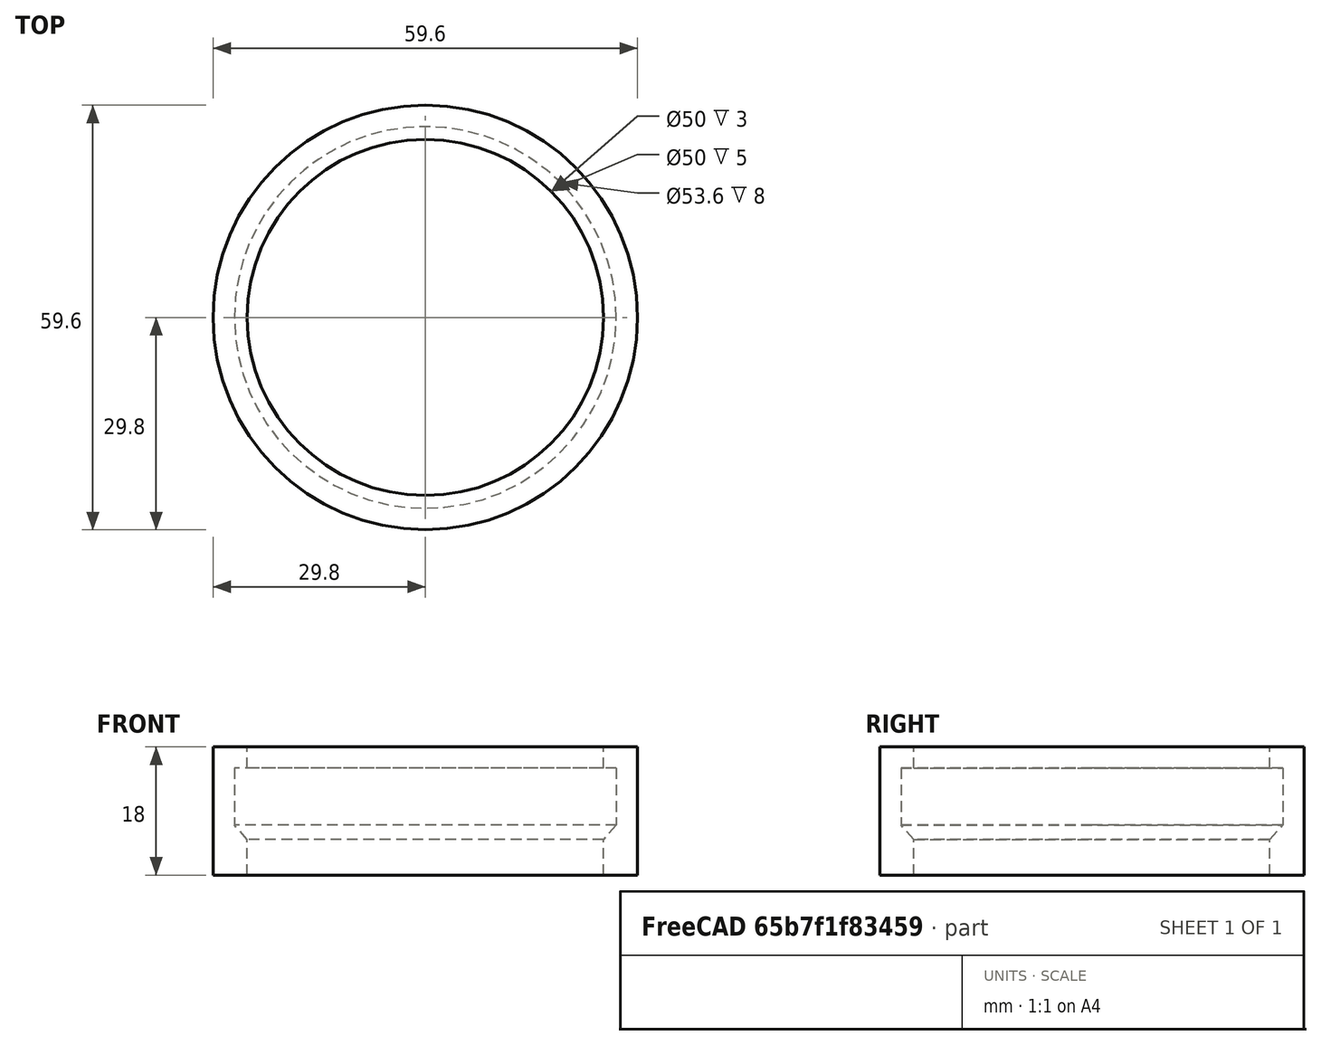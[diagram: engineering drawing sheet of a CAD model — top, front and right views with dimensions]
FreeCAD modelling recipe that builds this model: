
FCSTD DOCUMENT  (FreeCAD 1.1R39748 (Git))
Label: горло
License: All rights reserved
LicenseURL: https://en.wikipedia.org/wiki/All_rights_reserved
objects: App::Point×1, Sketcher::SketchObject×1, PartDesign::Revolution×1, PartDesign::Body×1
note: 6 computed .brp shape members not serialized (recipe doc carries the construction recipe); baked Part::Feature solids carry a one-line shape summary decoded from their .brp

FEATURE [App::Point] Origin001
  Role = Origin
FEATURE [Sketcher::SketchObject] Sketch
  ArcFitTolerance = 1e-06
  AttachmentSupport = -> [XZ_Plane]
  ExternalTypes = [0]
  FullyConstrained = true
  MakeInternals = false
  MapMode = 5
  Placement = pos=(0,0,0) rot=(1,0,0;1.5708rad)
  expr: Constraints[23] = 63 / 2 - 1.8
  expr: Constraints[2] = 50 / 2
  sketch-geometry (8):
    g0: LineSegment StartX=25 StartY=0 StartZ=0 EndX=25 EndY=5 EndZ=0
    g1: LineSegment StartX=29.7 StartY=17.7 StartZ=0 EndX=29.7 EndY=9.7 EndZ=0
    g2: LineSegment StartX=29.7 StartY=9.7 StartZ=0 EndX=25 EndY=5 EndZ=0
    g3: LineSegment StartX=29.7 StartY=17.7 StartZ=0 EndX=25 EndY=17.7 EndZ=0
    g4: LineSegment StartX=25 StartY=17.7 StartZ=0 EndX=25 EndY=20.7 EndZ=0
    g5: LineSegment StartX=25 StartY=20.7 StartZ=0 EndX=32.7 EndY=20.7 EndZ=0
    g6: LineSegment StartX=32.7 StartY=20.7 StartZ=0 EndX=32.7 EndY=0 EndZ=0
    g7: LineSegment StartX=32.7 StartY=0 StartZ=0 EndX=25 EndY=0 EndZ=0
  constraints (24):
    c: PointOnObject(g0,g-1)
    c: Vertical(g0)
    c: Distance(g0,g-1) = 25
    c: Vertical(g1)
    c: Coincident(g2,g0)
    c: Coincident(g1,g2)
    c: Distance(g1,g1) = 8
    c: Coincident(g3,g1)
    c: Horizontal(g3)
    c: DistanceX(g-1,g3) = 25
    c: Coincident(g4,g3)
    c: Vertical(g4)
    c: Coincident(g5,g4)
    c: Horizontal(g5)
    c: Coincident(g6,g5)
    c: PointOnObject(g6,g-1)
    c: Vertical(g6)
    c: Coincident(g7,g6)
    c: Coincident(g7,g0)
    c: Distance(g3,g4) = 3
    c: DistanceX(g1,g6) = 3
    c: DistanceY(g0,g0) = 5
    c: Angle(g0,g2) = 2.35619
    c: DistanceX(g-1,g1) = 29.7
FEATURE [PartDesign::Revolution] Revolution
  Angle = 360
  Angle2 = 60
  Axis = (0,2e-16,1)
  Base = (0,0,0)
  Placement = pos=(0,0,0) rot=(1,0,0;1.5708rad)
  Profile = -> Sketch
  ReferenceAxis = -> Sketch [V_Axis]
  Reversed = true
  Suppressed = false
  Type = 0
FEATURE [PartDesign::Body] Body
  AllowCompound = false
  Group = -> [Sketch,Revolution]
  Origin = -> Origin
  Tip = -> Revolution
